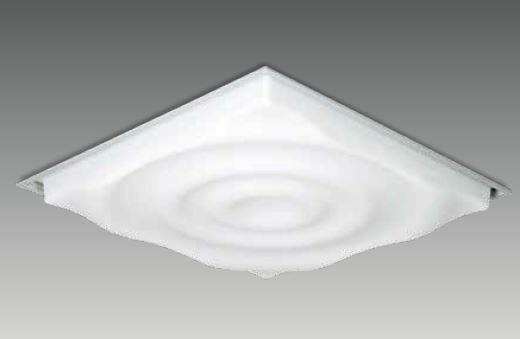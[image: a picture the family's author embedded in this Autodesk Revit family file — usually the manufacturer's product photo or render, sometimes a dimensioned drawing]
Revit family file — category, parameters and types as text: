
# Revit family: G 6060 DRO
name_source: partatom
category: Lighting Fixtures
revit_build: Autodesk Revit 2017 (Build: 20160225_1515(x64)
units: mm (PartAtom-declared; Revit-internal decimal feet)

## family parameters
Always vertical = Yes
Cut with Voids When Loaded = No
Host = Ceiling
Light Source = Yes
OmniClass Number = 23.80.70.11
OmniClass Title = Luminaries for Internal Lighting
Part Type = Normal
Room Calculation Point = No
Round Connector Dimension = Use Diameter
Shared = No

## types (4) — shared parameters
Color Filter = 16777215
Dimming Lamp Color Temperature Shift = <None>
Emit Shape Visible in Rendering = No
Emit from Rectangle Length = 540 mm  [stored 1.77165 ft]
Emit from Rectangle Width = 540 mm  [stored 1.77165 ft]
Light Source Symbol Size = 610 mm
Manufacturer = ARLIGHT
Type Image = G 6060 DRO.JPG

## per-type parameters (varying)
| type | Wattage Comments |
| GDRO.6060.36.30 | 36 |
| GDRO.6060.36.40 | 36 |
| GDRO.6060.28.30 | 28 |
| GDRO.6060.28.40 | 28 |

note: [stored X ft] marks values corroborated as IEEE doubles in the binary element streams (Revit-internal decimal feet)

## geometry (parser evidence)
native form markers: Sweep x2
no freeform markers — native parametric forms only
